# Revit family: SDP-8082 Видеокамера дальнего обзора_RV17_LOD400
name_source: partatom
category: Устройства связи
revit_build: Autodesk Revit 2017 (Build: 20170118_1100(x64)
units: mm (PartAtom-declared; Revit-internal decimal feet)

## family parameters
Всегда вертикально = Нет
На основе рабочей плоскости = Нет
Общий = Нет
При загрузке вырезать с полостями = Нет
Размер круглого соединителя = Использовать диаметр
Сохранять ориентацию аннотаций = Нет
Тип детали = Нормальный
Точка расчета площади = Нет

## types (1)
- SDP-8082
    ADSK_URL страницы изделия = https://stilsoft.ru
    ADSK_Единица измерения = шт.
    ADSK_Завод-изготовитель = ООО «Основа Безопасности»
    ADSK_Количество = 1
    ADSK_Марка = СТВФ.426459.036
    ADSK_Масса = 11
    ADSK_Наименование = Видеокамера дальнего обзора SDP-8082
    ADSK_Размер_Высота = 166 мм
    ADSK_Размер_Длина = 586 мм
    ADSK_Размер_Ширина = 186 мм
    d_короба = 20 мм
    Диапазон диафрагмы (F-стоп) = 1,8 – 360
    Матрица = 1/1,8" CMOS
    Минимальная дальность наблюдения, не менее, м = 50
    Мощность = 6
    Напряжение = 12
    Напряжение электропитания постоянного тока видеокамеры, В = 12
    Напряжение электропитания постоянного тока дополнительного обогрева, В = 24
    Обнаружение и распознавание цели типа “автомобиль”, до, м = 3000 мм
    Обнаружение и распознавание цели типа “человек”, до, м = 2000
    Объектив = Моторизованный трансфокатор
    Потребляемая мощность видеокамеры, Вт = 6 (макс. 9 при включении ИК фильтра)
    Потребляемая мощность встроенного обогрева, Вт = 30
    Разрешение матрицы, пикс = 2592х1944
    Режим «День/ночь» = Механический ИК-фильтр с автопереключением
    Режим работы = непрерывный
    Скорость передачи = 200Кб/сек – 12МБ/сек
    Скорость электронного затвора, с = 1-1/50,000
    Тип крепления объектива = C/СS
    Трехмерное шумоподавление (DNR) = Есть(3D)
    Угол поля зрения по вертикали, град. = 32,8 – 2,3
    Угол поля зрения по горизонтали, град. = 43,2 – 3,1
    Угол поля зрения по диагонали, град. = 52,9 – 3,8
    Фокусное расстояние, мм = от 8 до 120
    Формат сжатия = H.265
    Чувствительность цвет, Люкс = 0,01 / F1.2
    Чувствительность ч/б, Люкс = 0,001 / F1.2
    Широкий динамический диапазон (WDR) = Есть(120Дб)
